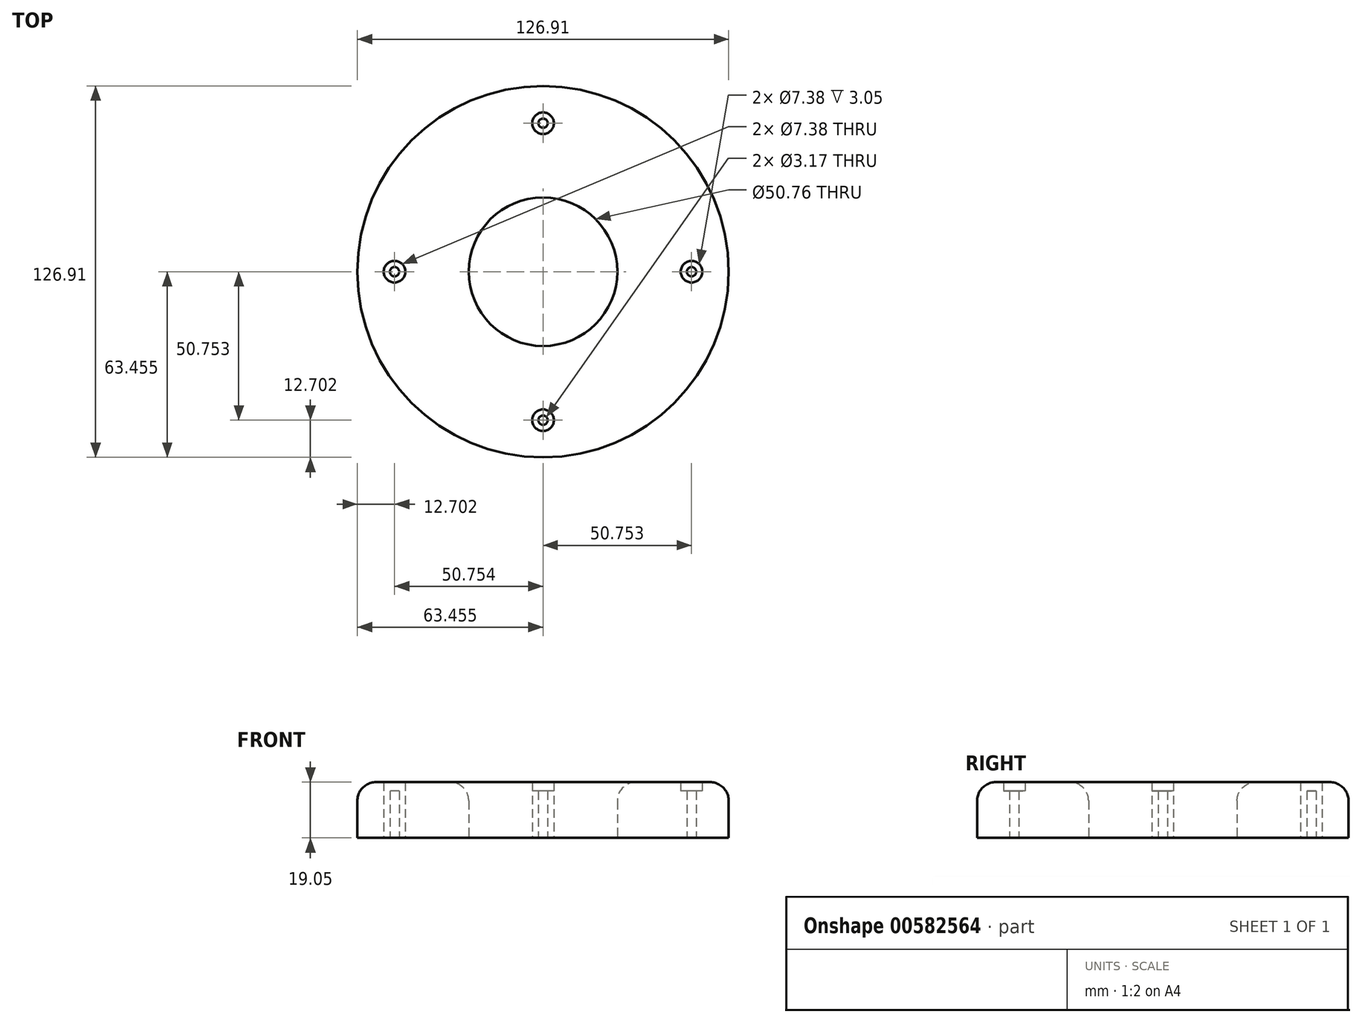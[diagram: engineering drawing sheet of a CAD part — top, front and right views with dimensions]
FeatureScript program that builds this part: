
annotation { "Feature Type Name" : "Feature", "Feature Type Description" : "" }
export const myFeature = defineFeature(function(context is Context, id is Id, definition is map)
    precondition{}
    {
        {
            var Q0;
            Q0=qCreatedBy(makeId("Top.planeOp"),FACE);
            var sketch = newSketch(context, id + "F0", { "sketchPlane" : qUnion([Q0])});
            skCircle(sketch, "E0", {"center": v(73, 73.26) * mm, "radius": 63.45 * mm});
            skCircle(sketch, "E1", {"center": v(73, 73.26) * mm, "radius": 25.38 * mm});
            skCircle(sketch, "E2.MirrorC", {"center": v(73, 124) * mm, "radius": 1.59 * mm});
            skCircle(sketch, "E3.MirrorC", {"center": v(73, 22.5) * mm, "radius": 1.59 * mm});
            skCircle(sketch, "E4.MirrorC", {"center": v(22.25, 73.26) * mm, "radius": 1.59 * mm});
            skCircle(sketch, "E5.MirrorC", {"center": v(123.76, 73.26) * mm, "radius": 1.59 * mm});
            skCircle(sketch, "E6", {"center": v(123.76, 73.26) * mm, "radius": 3.69 * mm});
            skCircle(sketch, "E7", {"center": v(73, 124) * mm, "radius": 3.69 * mm});
            skCircle(sketch, "E8", {"center": v(22.25, 73.26) * mm, "radius": 3.69 * mm});
            skCircle(sketch, "E9", {"center": v(73, 22.5) * mm, "radius": 3.69 * mm});
            skSolve(sketch);
        }
        {
            var Q0;
            Q0=makeQuery(id+"F0.imprint","IMPRINT",FACE,{"disambiguationData":[TD([[makeQuery(id+"F0.imprint","IMPRINT",EDGE,{"derivedFrom":sQuery(id+"F0.wireOp",EDGE,"E0")}),1.0]])]});
            extrude(context, id + "F1", {"entities" : qUnion([Q0]), "depth" : 19.05 * mm, "offsetDistance" : 25.4 * mm});
        }
        {
            var Q0;
            Q0=makeQuery(id+"F0.imprint","IMPRINT",FACE,{"disambiguationData":[TD([[makeQuery(id+"F0.imprint","IMPRINT",EDGE,{"derivedFrom":sQuery(id+"F0.wireOp",EDGE,"E4.MirrorC")}),1.0]])]});
            var Q1;
            Q1=makeQuery(id+"F0.imprint","IMPRINT",FACE,{"disambiguationData":[TD([[makeQuery(id+"F0.imprint","IMPRINT",EDGE,{"derivedFrom":sQuery(id+"F0.wireOp",EDGE,"E3.MirrorC")}),-1.0]])]});
            var Q2;
            Q2=makeQuery(id+"F0.imprint","IMPRINT",FACE,{"disambiguationData":[TD([[makeQuery(id+"F0.imprint","IMPRINT",EDGE,{"derivedFrom":sQuery(id+"F0.wireOp",EDGE,"E5.MirrorC")}),-1.0]])]});
            var Q3;
            Q3=makeQuery(id+"F0.imprint","IMPRINT",FACE,{"disambiguationData":[TD([[makeQuery(id+"F0.imprint","IMPRINT",EDGE,{"derivedFrom":sQuery(id+"F0.wireOp",EDGE,"E2.MirrorC")}),1.0]])]});
            extrude(context, id + "F2", {"entities" : qUnion([Q0, Q1, Q2, Q3]), "operationType" : NewBodyOperationType.ADD, "depth" : 16 * mm, "offsetDistance" : 25.4 * mm});
        }
        {
            var Q0;
            Q0=makeQuery(id+"F1.opExtrude","CAP_EDGE",EDGE,{"disambiguationData":[OSD([sQuery(id+"F0.wireOp",EDGE,"E0")])],"isStart":false});
            fillet(context, id + "F3", {"entities" : qUnion([Q0]), "radius" : 6.35 * mm, "tangentPropagation" : true, "allowEdgeOverflow" : false});
        }
        {
            var Q0;
            Q0=makeQuery(id+"F1.opExtrude","CAP_EDGE",EDGE,{"disambiguationData":[OSD([sQuery(id+"F0.wireOp",EDGE,"E1")])],"isStart":false});
            fillet(context, id + "F4", {"entities" : qUnion([Q0]), "radius" : 6.35 * mm, "tangentPropagation" : true, "allowEdgeOverflow" : false});
        }
    });
